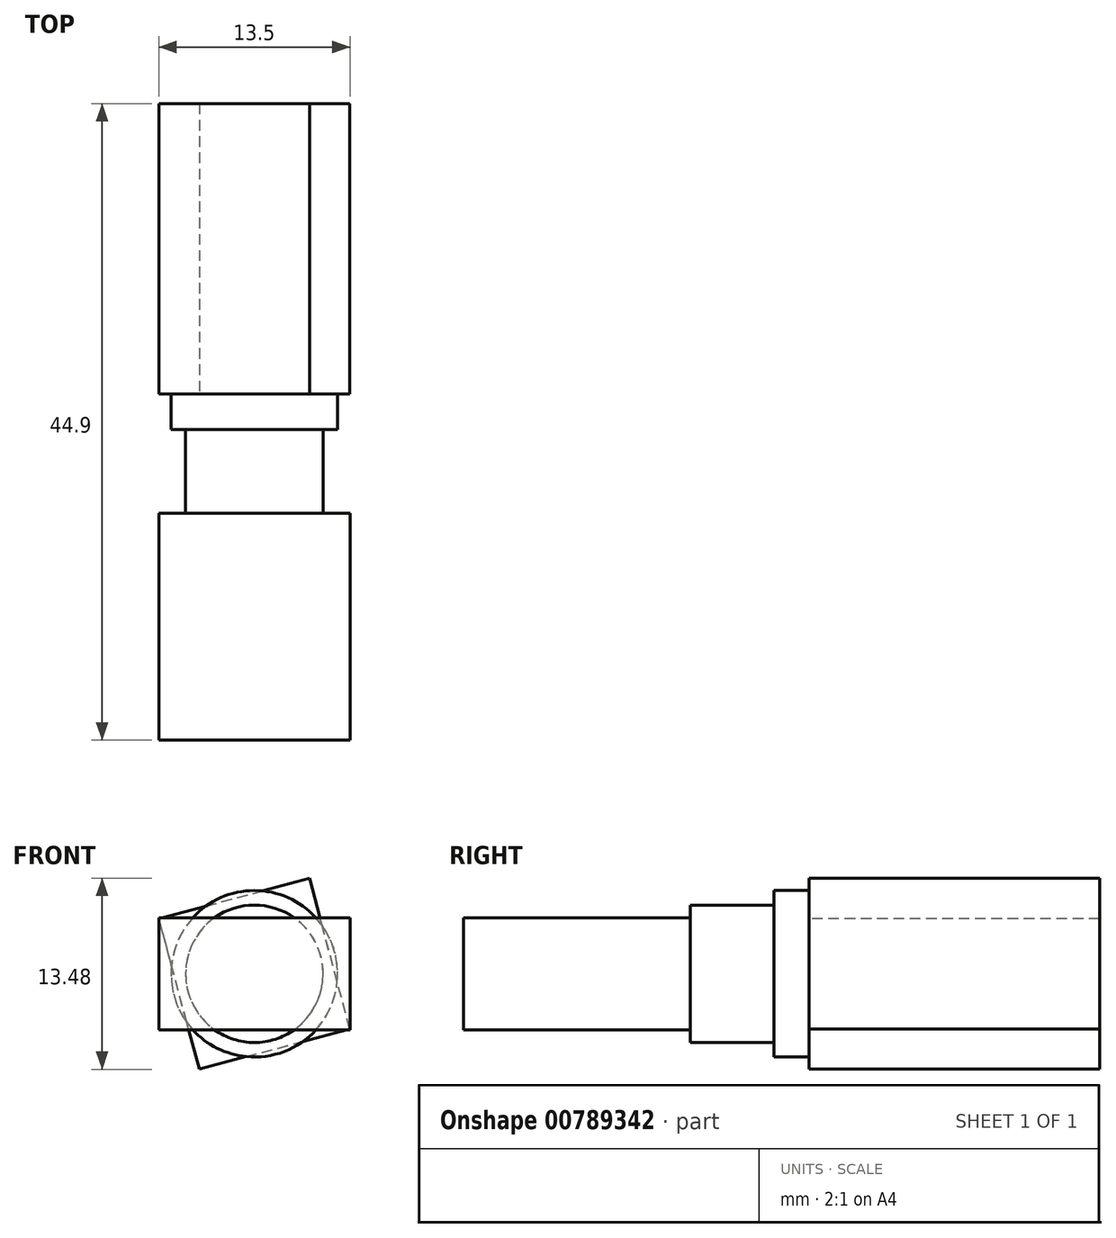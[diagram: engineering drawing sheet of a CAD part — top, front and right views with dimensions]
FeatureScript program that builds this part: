
annotation { "Feature Type Name" : "Feature", "Feature Type Description" : "" }
export const myFeature = defineFeature(function(context is Context, id is Id, definition is map)
    precondition{}
    {
        {
            var Q0;
            Q0=qCreatedBy(makeId("Front.planeOp"),FACE);
            var sketch = newSketch(context, id + "F0", { "sketchPlane" : qUnion([Q0])});
            skLineSegment(sketch, "E0.bottom", {"start": v(6.75, -3.95) * mm, "end": v(-6.75, -3.95) * mm});
            skLineSegment(sketch, "E0.top", {"start": v(6.75, 3.95) * mm, "end": v(-6.75, 3.95) * mm});
            skLineSegment(sketch, "E0.left", {"start": v(6.75, -3.95) * mm, "end": v(6.75, 3.95) * mm});
            skLineSegment(sketch, "E0.right", {"start": v(-6.75, -3.95) * mm, "end": v(-6.75, 3.95) * mm});
            skPoint(sketch, "E0.middle", {"position": v(0, 0) * mm});
            skCircle(sketch, "E1", {"center": v(0, 0) * mm, "radius": 4.85 * mm});
            skSolve(sketch);
        }
        {
            var Q0;
            {var subQ0=sQuery(id+"F0.wireOp",EDGE,"E1");var subQ1=sQuery(id+"F0.wireOp",EDGE,"E0.bottom");var subQ2=makeQuery(id+"F0.imprint","INTERSECT",VERTEX,{"disambiguationData":[OD(0.0)],"derivedFrom":[subQ1,subQ0]});Q0=makeQuery(id+"F0.imprint","IMPRINT",FACE,{"disambiguationData":[TD([[makeQuery(id+"F0.imprint","IMPRINT",EDGE,{"disambiguationData":[TD([[subQ2,-1.0]])],"derivedFrom":subQ1}),-1.0]])]});}
            var Q1;
            {var subQ0=sQuery(id+"F0.wireOp",EDGE,"E1");var subQ1=sQuery(id+"F0.wireOp",EDGE,"E0.bottom");var subQ2=makeQuery(id+"F0.imprint","INTERSECT",VERTEX,{"disambiguationData":[OD(0.0)],"derivedFrom":[subQ1,subQ0]});Q1=makeQuery(id+"F0.imprint","IMPRINT",FACE,{"disambiguationData":[TD([[makeQuery(id+"F0.imprint","IMPRINT",EDGE,{"disambiguationData":[TD([[subQ2,-1.0]])],"derivedFrom":subQ1}),1.0]])]});}
            var Q2;
            {var subQ0=sQuery(id+"F0.wireOp",EDGE,"E1");var subQ1=sQuery(id+"F0.wireOp",EDGE,"E0.top");var subQ2=makeQuery(id+"F0.imprint","INTERSECT",VERTEX,{"disambiguationData":[OD(0.0)],"derivedFrom":[subQ1,subQ0]});Q2=makeQuery(id+"F0.imprint","IMPRINT",FACE,{"disambiguationData":[TD([[makeQuery(id+"F0.imprint","IMPRINT",EDGE,{"disambiguationData":[TD([[subQ2,-1.0]])],"derivedFrom":subQ1}),-1.0]])]});}
            var Q3;
            Q3=sQuery(id+"F0.wireOp",EDGE,"E1");
            extrude(context, id + "F1", {"entities" : qUnion([Q0, Q1, Q2]), "surfaceEntities" : qUnion([Q3]), "oppositeDirection" : true, "depth" : 5.9 * mm, "offsetDistance" : 25 * mm});
        }
        {
            var Q0;
            {var subQ0=sQuery(id+"F0.wireOp",EDGE,"E0.right");Q0=makeQuery(id+"F0.imprint","IMPRINT",FACE,{"disambiguationData":[TD([[makeQuery(id+"F0.imprint","IMPRINT",EDGE,{"derivedFrom":subQ0}),-1.0]])]});}
            var Q1;
            {var subQ0=sQuery(id+"F0.wireOp",EDGE,"E1");var subQ1=sQuery(id+"F0.wireOp",EDGE,"E0.bottom");var subQ2=makeQuery(id+"F0.imprint","INTERSECT",VERTEX,{"disambiguationData":[OD(0.0)],"derivedFrom":[subQ1,subQ0]});Q1=makeQuery(id+"F0.imprint","IMPRINT",FACE,{"disambiguationData":[TD([[makeQuery(id+"F0.imprint","IMPRINT",EDGE,{"disambiguationData":[TD([[subQ2,-1.0]])],"derivedFrom":subQ1}),-1.0]])]});}
            var Q2;
            {var subQ0=sQuery(id+"F0.wireOp",EDGE,"E0.left");Q2=makeQuery(id+"F0.imprint","IMPRINT",FACE,{"disambiguationData":[TD([[makeQuery(id+"F0.imprint","IMPRINT",EDGE,{"derivedFrom":subQ0}),1.0]])]});}
            extrude(context, id + "F2", {"entities" : qUnion([Q0, Q1, Q2]), "operationType" : NewBodyOperationType.ADD, "depth" : 16 * mm, "offsetDistance" : 25 * mm});
        }
        {
            var Q0;
            Q0=makeQuery(id+"F1.opExtrude","CAP_FACE",FACE,{"disambiguationData":[OSD([sQuery(id+"F0.wireOp",EDGE,"E1")])],"isStart":false});
            var sketch = newSketch(context, id + "F3", { "sketchPlane" : qUnion([Q0])});
            skCircle(sketch, "E2", {"center": v(0, 0) * mm, "radius": 5.88 * mm});
            skSolve(sketch);
        }
        {
            var Q0;
            Q0=makeQuery(id+"F3.imprint","IMPRINT",FACE,{"disambiguationData":[TD([[makeQuery(id+"F3.imprint","IMPRINT",EDGE,{"derivedFrom":sQuery(id+"F3.wireOp",EDGE,"E2")}),1.0]])]});
            var Q1;
            Q1=makeQuery(id+"F3.imprint","IMPRINT",FACE,{"disambiguationData":[TD([[makeQuery(id+"F3.imprint","IMPRINT",EDGE,{"derivedFrom":makeQuery(id+"F1.opExtrude","CAP_EDGE",EDGE,{"disambiguationData":[OSD([sQuery(id+"F0.wireOp",EDGE,"E1")])],"isStart":false})}),-1.0]])]});
            var Q2;
            Q2=sQuery(id+"F3.wireOp",EDGE,"E2");
            extrude(context, id + "F4", {"entities" : qUnion([Q0, Q1]), "operationType" : NewBodyOperationType.ADD, "surfaceEntities" : qUnion([Q2]), "depth" : 2.5 * mm, "offsetDistance" : 25 * mm});
        }
        {
            var Q0;
            Q0=makeQuery(id+"F4.opExtrude","CAP_FACE",FACE,{"disambiguationData":[OSD([sQuery(id+"F3.wireOp",EDGE,"E2")])],"isStart":false});
            var sketch = newSketch(context, id + "F5", { "sketchPlane" : qUnion([Q0])});
            skLineSegment(sketch, "E3.bottom", {"start": v(3.89, -6.74) * mm, "end": v(-6.74, -3.89) * mm});
            skLineSegment(sketch, "E3.top", {"start": v(6.74, 3.89) * mm, "end": v(-3.89, 6.74) * mm});
            skLineSegment(sketch, "E3.left", {"start": v(3.89, -6.74) * mm, "end": v(6.74, 3.89) * mm});
            skLineSegment(sketch, "E3.right", {"start": v(-6.74, -3.89) * mm, "end": v(-3.89, 6.74) * mm});
            skPoint(sketch, "E3.middle", {"position": v(0, 0) * mm});
            skLineSegment(sketch, "E4", {"start": v(0, 0) * mm, "end": v(-6.74, -3.89) * mm, "construction": true});
            skSolve(sketch);
        }
        {
            var Q0;
            Q0 = qSketchRegion(id + "F5", true);
            extrude(context, id + "F6", {"entities" : qUnion([Q0]), "operationType" : NewBodyOperationType.ADD, "depth" : 20.5 * mm, "offsetDistance" : 25 * mm});
        }
    });
